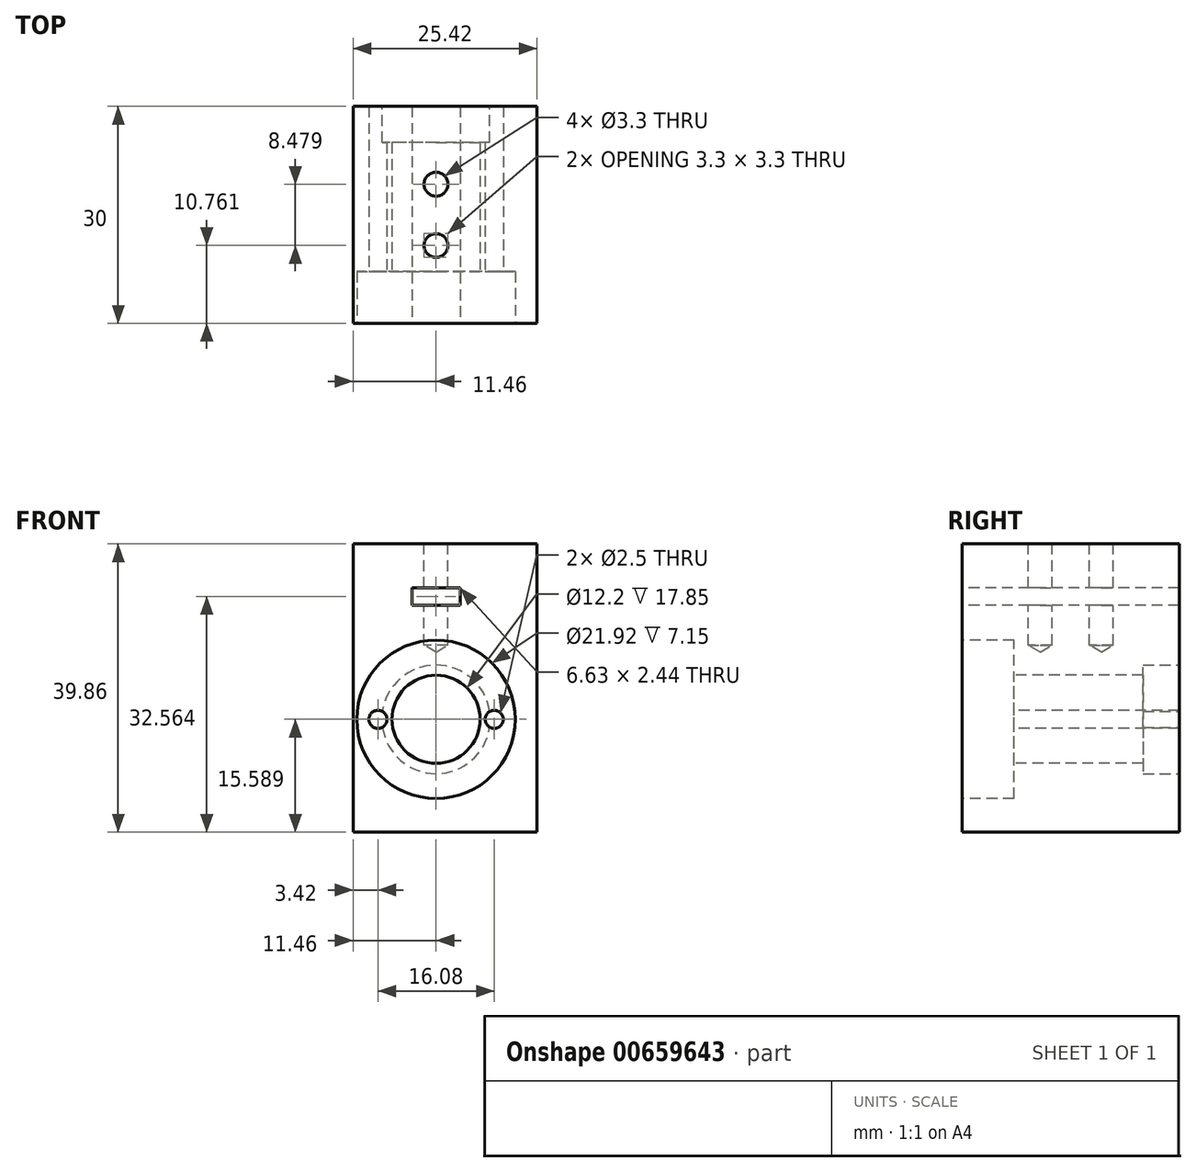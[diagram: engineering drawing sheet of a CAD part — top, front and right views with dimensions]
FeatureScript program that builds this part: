
annotation { "Feature Type Name" : "Feature", "Feature Type Description" : "" }
export const myFeature = defineFeature(function(context is Context, id is Id, definition is map)
    precondition{}
    {
        {
            var Q0;
            Q0=qCreatedBy(makeId("Top.planeOp"),FACE);
            var sketch = newSketch(context, id + "F0", { "sketchPlane" : qUnion([Q0])});
            skLineSegment(sketch, "E0.bottom", {"start": v(12.7, 15) * mm, "end": v(-12.7, 15) * mm});
            skLineSegment(sketch, "E0.top", {"start": v(12.7, -15) * mm, "end": v(-12.7, -15) * mm});
            skLineSegment(sketch, "E0.left", {"start": v(12.7, 15) * mm, "end": v(12.7, -15) * mm});
            skLineSegment(sketch, "E0.right", {"start": v(-12.7, 15) * mm, "end": v(-12.7, -15) * mm});
            skPoint(sketch, "E0.middle", {"position": v(0, 0) * mm});
            skSolve(sketch);
        }
        {
            var Q0;
            Q0 = qSketchRegion(id + "F0", true);
            extrude(context, id + "F1", {"entities" : qUnion([Q0]), "depth" : 39.86 * mm, "offsetDistance" : 25 * mm});
        }
        {
            var Q0;
            Q0=makeQuery(id+"F1.opExtrude","CAP_FACE",FACE,{"disambiguationData":[OSD([sQuery(id+"F0.wireOp",EDGE,"E0.bottom"),sQuery(id+"F0.wireOp",EDGE,"E0.top"),sQuery(id+"F0.wireOp",EDGE,"E0.left"),sQuery(id+"F0.wireOp",EDGE,"E0.right")])],"isStart":false});
            var sketch = newSketch(context, id + "F2", { "sketchPlane" : qUnion([Q0])});
            skLineSegment(sketch, "E1", {"start": v(-12.7, 0) * mm, "end": v(-1.25, 0) * mm, "construction": true});
            skLineSegment(sketch, "E2.bottom", {"start": v(-1.25, 4.24) * mm, "end": v(-1.25, 4.24) * mm});
            skLineSegment(sketch, "E2.top", {"start": v(-1.25, -4.24) * mm, "end": v(-1.25, -4.24) * mm});
            skLineSegment(sketch, "E2.left", {"start": v(-1.25, 4.24) * mm, "end": v(-1.25, -4.24) * mm});
            skLineSegment(sketch, "E2.right", {"start": v(-1.25, 4.24) * mm, "end": v(-1.25, -4.24) * mm, "construction": true});
            skPoint(sketch, "E2.middle", {"position": v(-1.25, 0) * mm});
            skPoint(sketch, "E3", {"position": v(-1.25, 4.24) * mm});
            skPoint(sketch, "E4", {"position": v(-1.25, -4.24) * mm});
            skLineSegment(sketch, "E5", {"start": v(-1.25, -4.24) * mm, "end": v(-1.25, -15) * mm, "construction": true});
            skSolve(sketch);
        }
        {
            var Q0;
            Q0=makeQuery(id+"F1.opExtrude","SWEPT_FACE",FACE,{"disambiguationData":[OSD([sQuery(id+"F0.wireOp",EDGE,"E0.top")])]});
            var sketch = newSketch(context, id + "F3", { "sketchPlane" : qUnion([Q0])});
            skLineSegment(sketch, "E6.0.0", {"start": v(-12.7, 39.86) * mm, "end": v(12.7, 39.86) * mm});
            skLineSegment(sketch, "E6.0.2", {"start": v(12.7, 39.86) * mm, "end": v(-12.7, 39.86) * mm});
            skPoint(sketch, "E7.0", {"position": v(-1.25, 39.86) * mm});
            skLineSegment(sketch, "E8", {"start": v(-1.25, 39.86) * mm, "end": v(-1.25, 32.56) * mm, "construction": true});
            skLineSegment(sketch, "E9", {"start": v(-1.25, 39.86) * mm, "end": v(-1.25, 15.59) * mm, "construction": true});
            skLineSegment(sketch, "E10", {"start": v(-1.25, 15.59) * mm, "end": v(-7.35, 15.59) * mm, "construction": true});
            skLineSegment(sketch, "E11", {"start": v(-1.25, 15.59) * mm, "end": v(-12.21, 15.59) * mm, "construction": true});
            skLineSegment(sketch, "E12.bottom", {"start": v(-4.56, 33.79) * mm, "end": v(2.06, 33.79) * mm});
            skLineSegment(sketch, "E12.top", {"start": v(-4.56, 31.34) * mm, "end": v(2.06, 31.34) * mm});
            skLineSegment(sketch, "E12.left", {"start": v(-4.56, 33.79) * mm, "end": v(-4.56, 31.34) * mm});
            skLineSegment(sketch, "E12.right", {"start": v(2.06, 33.79) * mm, "end": v(2.06, 31.34) * mm});
            skPoint(sketch, "E12.middle", {"position": v(-1.25, 32.56) * mm});
            skLineSegment(sketch, "E13.bottom", {"start": v(6.79, 15.59) * mm, "end": v(-9.29, 15.59) * mm});
            skLineSegment(sketch, "E13.top", {"start": v(6.79, 15.59) * mm, "end": v(-9.29, 15.59) * mm, "construction": true});
            skLineSegment(sketch, "E13.left", {"start": v(6.79, 15.59) * mm, "end": v(6.79, 15.59) * mm});
            skLineSegment(sketch, "E13.right", {"start": v(-9.29, 15.59) * mm, "end": v(-9.29, 15.59) * mm});
            skPoint(sketch, "E13.middle", {"position": v(-1.25, 15.59) * mm});
            skPoint(sketch, "E14", {"position": v(-9.29, 15.59) * mm});
            skPoint(sketch, "E15", {"position": v(6.79, 15.59) * mm});
            skCircle(sketch, "E16", {"center": v(-1.25, 15.59) * mm, "radius": 10.96 * mm});
            skSolve(sketch);
        }
        {
            var Q0;
            Q0=sQuery(id+"F2.wireOp",VERTEX,"E3");
            var Q1;
            Q1=sQuery(id+"F2.wireOp",VERTEX,"E4");
            var Q2;
            Q2=makeQuery(id+"F1.opExtrude","SWEPT_BODY",BODY,{"disambiguationData":[OSD([sQuery(id+"F0.wireOp",EDGE,"E0.bottom"),sQuery(id+"F0.wireOp",EDGE,"E0.top"),sQuery(id+"F0.wireOp",EDGE,"E0.left"),sQuery(id+"F0.wireOp",EDGE,"E0.right")])]});
            hole(context, id + "F4", {"style" : HoleStyle.SIMPLE, "endStyle" : HoleEndStyle.BLIND, "standardTappedOrClearance" : lookupTablePath({ "standard" : "ISO", "fit" : "Normal", "size" : "M3", "type" : "Clearance" }), "standardBlindInLast" : lookupTablePath({ "fit" : "Standard", "standard" : "ISO", "size" : "M3", "type" : "Clearance" }), "holeDiameter" : 3.3 * mm, "majorDiameter" : 5 * mm, "holeDepth" : 14 * mm, "tappedDepth" : 12 * mm, "tapClearance" : 3, "startFromSketch" : true, "locations" : qUnion([Q0, Q1]), "scope" : qUnion([Q2])});
        }
        {
            var Q0;
            Q0=makeQuery(id+"F3.imprint","IMPRINT",FACE,{"disambiguationData":[TD([[makeQuery(id+"F3.imprint","IMPRINT",EDGE,{"derivedFrom":sQuery(id+"F3.wireOp",EDGE,"E12.bottom")}),-1.0]])]});
            extrude(context, id + "F5", {"entities" : qUnion([Q0]), "operationType" : NewBodyOperationType.REMOVE, "endBound" : BoundingType.THROUGH_ALL, "oppositeDirection" : true, "depth" : 25 * mm, "offsetDistance" : 25 * mm});
        }
        {
            var Q0;
            Q0=sQuery(id+"F3.wireOp",VERTEX,"E10.start");
            var Q1;
            Q1=makeQuery(id+"F1.opExtrude","SWEPT_BODY",BODY,{"disambiguationData":[OSD([sQuery(id+"F0.wireOp",EDGE,"E0.bottom"),sQuery(id+"F0.wireOp",EDGE,"E0.top"),sQuery(id+"F0.wireOp",EDGE,"E0.left"),sQuery(id+"F0.wireOp",EDGE,"E0.right")])]});
            hole(context, id + "F6", {"style" : HoleStyle.SIMPLE, "endStyle" : HoleEndStyle.THROUGH, "holeDiameter" : 12.2 * mm, "majorDiameter" : 5 * mm, "tappedDepth" : 12 * mm, "tapClearance" : 3, "startFromSketch" : true, "locations" : qUnion([Q0]), "scope" : qUnion([Q1])});
        }
        {
            var Q0;
            Q0=sQuery(id+"F3.wireOp",VERTEX,"E14");
            var Q1;
            Q1=sQuery(id+"F3.wireOp",VERTEX,"E15");
            var Q2;
            Q2=makeQuery(id+"F1.opExtrude","SWEPT_BODY",BODY,{"disambiguationData":[OSD([sQuery(id+"F0.wireOp",EDGE,"E0.bottom"),sQuery(id+"F0.wireOp",EDGE,"E0.top"),sQuery(id+"F0.wireOp",EDGE,"E0.left"),sQuery(id+"F0.wireOp",EDGE,"E0.right")])]});
            hole(context, id + "F7", {"style" : HoleStyle.SIMPLE, "endStyle" : HoleEndStyle.THROUGH, "standardTappedOrClearance" : lookupTablePath({ "standard" : "ISO", "engagement" : "75%", "pitch" : "0.5 mm", "size" : "M3", "type" : "Tapped" }), "standardBlindInLast" : lookupTablePath({ "standard" : "ISO", "engagement" : "75%", "pitch" : "0.5 mm", "size" : "M3", "type" : "Tapped" }), "holeDiameter" : 2.5 * mm, "majorDiameter" : 3 * mm, "showTappedDepth" : true, "tappedDepth" : 12 * mm, "tapClearance" : 3, "startFromSketch" : true, "locations" : qUnion([Q0, Q1]), "scope" : qUnion([Q2])});
        }
        {
            var Q0;
            Q0=makeQuery(id+"F3.imprint","IMPRINT",FACE,{"disambiguationData":[TD([[makeQuery(id+"F3.imprint","IMPRINT",EDGE,{"derivedFrom":sQuery(id+"F3.wireOp",EDGE,"E16")}),1.0]])]});
            extrude(context, id + "F8", {"entities" : qUnion([Q0]), "operationType" : NewBodyOperationType.REMOVE, "oppositeDirection" : true, "depth" : 7.15 * mm, "offsetDistance" : 25 * mm});
        }
        {
            var Q0;
            Q0=makeQuery(id+"F1.opExtrude","SWEPT_FACE",FACE,{"disambiguationData":[OSD([sQuery(id+"F0.wireOp",EDGE,"E0.bottom")])]});
            var sketch = newSketch(context, id + "F9", { "sketchPlane" : qUnion([Q0])});
            skPoint(sketch, "E17.0", {"position": v(1.25, 15.59) * mm});
            skCircle(sketch, "E18", {"center": v(1.25, 15.59) * mm, "radius": 7.5 * mm});
            skSolve(sketch);
        }
        {
            var Q0;
            Q0 = qSketchRegion(id + "F9", true);
            extrude(context, id + "F10", {"entities" : qUnion([Q0]), "operationType" : NewBodyOperationType.REMOVE, "oppositeDirection" : true, "depth" : 5 * mm, "offsetDistance" : 25 * mm});
        }
    });
